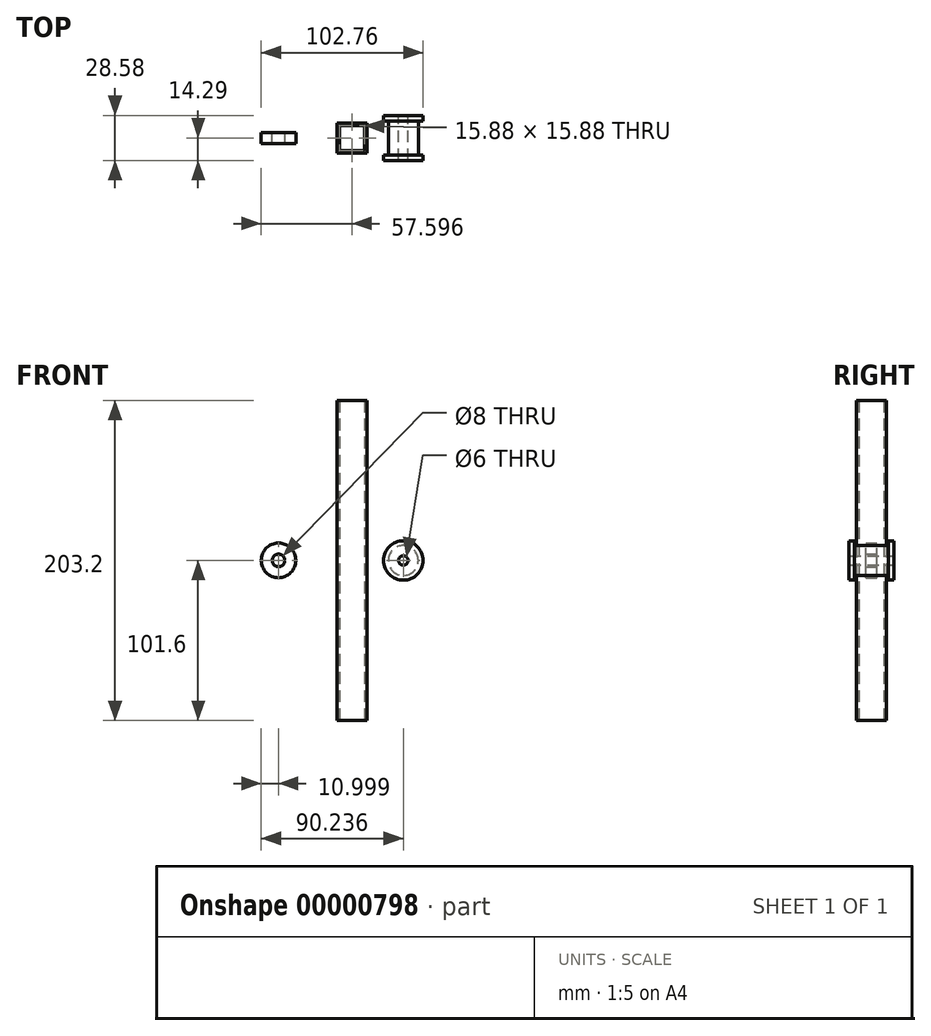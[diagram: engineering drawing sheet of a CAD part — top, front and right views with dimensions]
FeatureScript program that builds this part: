
annotation { "Feature Type Name" : "Feature", "Feature Type Description" : "" }
export const myFeature = defineFeature(function(context is Context, id is Id, definition is map)
    precondition{}
    {
        {
            var Q0;
            Q0=qCreatedBy(makeId("Top.planeOp"),FACE);
            var sketch = newSketch(context, id + "F0", { "sketchPlane" : qUnion([Q0])});
            skLineSegment(sketch, "E0.rect.bottom", {"start": v(-46.7, -9.53) * mm, "end": v(-65.76, -9.53) * mm});
            skLineSegment(sketch, "E0.rect.top", {"start": v(-46.7, 9.53) * mm, "end": v(-65.76, 9.53) * mm});
            skLineSegment(sketch, "E0.rect.left", {"start": v(-46.7, -9.53) * mm, "end": v(-46.7, 9.53) * mm});
            skLineSegment(sketch, "E0.rect.right", {"start": v(-65.76, -9.53) * mm, "end": v(-65.76, 9.53) * mm});
            skPoint(sketch, "E0.rect.middle", {"position": v(-56.23, 0) * mm});
            skLineSegment(sketch, "E1.rect.bottom", {"start": v(-48.3, 7.94) * mm, "end": v(-64.17, 7.94) * mm});
            skLineSegment(sketch, "E1.rect.top", {"start": v(-48.3, -7.94) * mm, "end": v(-64.17, -7.94) * mm});
            skLineSegment(sketch, "E1.rect.left", {"start": v(-48.3, 7.94) * mm, "end": v(-48.3, -7.94) * mm});
            skLineSegment(sketch, "E1.rect.right", {"start": v(-64.17, 7.94) * mm, "end": v(-64.17, -7.94) * mm});
            skSolve(sketch);
        }
        {
            var Q0;
            Q0=makeQuery(id+"F0.imprint","IMPRINT",FACE,{"disambiguationData":[TD([[makeQuery(id+"F0.imprint","IMPRINT",EDGE,{"derivedFrom":sQuery(id+"F0.wireOp",EDGE,"E0.rect.bottom")}),-1.0]])]});
            extrude(context, id + "F1", {"entities" : qUnion([Q0]), "endBound" : BoundingType.SYMMETRIC, "depth" : 203.2 * mm});
        }
        {
            var Q0;
            Q0=qCreatedBy(makeId("Top.planeOp"),FACE);
            var sketch = newSketch(context, id + "F2", { "sketchPlane" : qUnion([Q0])});
            skLineSegment(sketch, "E2.rect.bottom", {"start": v(-36.12, 14.29) * mm, "end": v(-26.6, 14.29) * mm});
            skLineSegment(sketch, "E2.rect.top", {"start": v(-36.12, -14.29) * mm, "end": v(-26.6, -14.29) * mm});
            skLineSegment(sketch, "E2.rect.left", {"start": v(-36.12, 14.29) * mm, "end": v(-36.12, 10.8) * mm});
            skLineSegment(sketch, "E2.rect.right", {"start": v(-26.6, 14.29) * mm, "end": v(-26.6, -14.29) * mm});
            skPoint(sketch, "E2.rect.middle", {"position": v(-31.36, 0) * mm});
            skLineSegment(sketch, "E3.rect.bottom", {"start": v(-33.12, 10.8) * mm, "end": v(-36.12, 10.8) * mm});
            skLineSegment(sketch, "E3.rect.top", {"start": v(-33.12, -10.8) * mm, "end": v(-36.12, -10.8) * mm});
            skLineSegment(sketch, "E3.rect.left", {"start": v(-33.12, 10.8) * mm, "end": v(-33.12, -10.8) * mm});
            skPoint(sketch, "E3.rect.middle", {"position": v(-36.12, 0) * mm});
            skPoint(sketch, "E3.rect.right.start.orphan", {"position": v(-39.12, 10.8) * mm});
            skLineSegment(sketch, "E4.trimOffspring", {"start": v(-36.12, -10.8) * mm, "end": v(-36.12, -14.29) * mm});
            skPoint(sketch, "E5.orphan", {"position": v(-39.12, -10.8) * mm});
            skLineSegment(sketch, "E6", {"start": v(-23.6, 14.29) * mm, "end": v(-23.6, -14.29) * mm, "construction": true});
            skSolve(sketch);
        }
        {
            var Q0;
            Q0=makeQuery(id+"F2.imprint","IMPRINT",FACE,{"disambiguationData":[TD([[makeQuery(id+"F2.imprint","IMPRINT",EDGE,{"derivedFrom":sQuery(id+"F2.wireOp",EDGE,"E2.rect.bottom")}),-1.0]])]});
            var Q1;
            Q1=sQuery(id+"F2.wireOp",EDGE,"E6");
            revolve(context, id + "F3", {"entities" : qUnion([Q0]), "axis" : qUnion([Q1]), "revolveType" : RevolveType.FULL});
        }
        {
            var Q0;
            Q0=qCreatedBy(makeId("Front.planeOp"),FACE);
            var sketch = newSketch(context, id + "F4", { "sketchPlane" : qUnion([Q0])});
            skCircle(sketch, "E7", {"center": v(-102.83, 0) * mm, "radius": 4 * mm});
            skCircle(sketch, "E8", {"center": v(-102.83, 0) * mm, "radius": 11 * mm});
            skSolve(sketch);
        }
        {
            var Q0;
            Q0=makeQuery(id+"F4.imprint","IMPRINT",FACE,{"disambiguationData":[TD([[makeQuery(id+"F4.imprint","IMPRINT",EDGE,{"derivedFrom":sQuery(id+"F4.wireOp",EDGE,"E7")}),-1.0]])]});
            extrude(context, id + "F5", {"entities" : qUnion([Q0]), "endBound" : BoundingType.SYMMETRIC, "depth" : 7 * mm});
        }
    });
